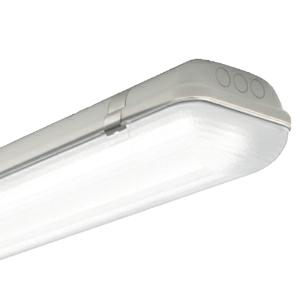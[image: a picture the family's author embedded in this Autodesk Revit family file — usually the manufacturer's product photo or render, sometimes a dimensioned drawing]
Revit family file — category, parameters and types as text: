
# Revit family: 3f_filippi_-_3f_linda_soft_3f_filippi_-_58753_-_3f_linda_led_soft_2x22w_dali_l1570
name_source: partatom
category: Lighting Fixtures
units: mm (PartAtom-declared; Revit-internal decimal feet)

## family parameters
Cut with Voids When Loaded = No
Host = Face
Light Source = No
Part Type = Normal
Room Calculation Point = No
Round Connector Dimension = Use Diameter
Shared = No

## types (1)
- 3F Filippi - 3F Linda Soft (1 x LED, 6835 lm, 49 W, 4000 K)
    Apparent Load = 49 VA
    Approval mark = CE
    CIE Flux Codes = 42 72 91 93 100
    Color Rendering = 80
    Color Temperature = 4000 K
    Control Gear = Electronic transformer
    Default Elevation = 1800 mm
    Description = ILLUMINOTECHNICAL
Luminous efficiency 100% (DLOR 93%, ULOR 7%).
Initial luminous flux of the luminaire 6835 lm.
Direct symmetric distribution.
Installation Interdistance Transv.D = 1.35 x hu - Long.D = 1.24 x hu.
Tabular UGR (CIE 117 - 4H-8H; S=0.25H; 70/50/20): RUG 23.7 - 21.8.
Beam angle: 131° - 111°.
Luminous efficacy 139 lm/W.
Lifetime (L93/B10): 30000 h. (tq+25°C)
Lifetime (L90/B10): 50000 h. (tq+25°C)
Lifetime (L85/B10): 80000 h. (tq+25°C)
Lifetime (L80/B10): 100000 h. (tq+25°C)
Lifetime (L85/B10): 50000 h. (tq+40°C)
Sudden decreased luminous flux after 50000 hours: 0% (C0).
Photobiological safety in compliance with IEC/TR 62778: RG0 risk exempt, (IEC 62471).
In compliance with IEC/EN 62722-2-1 - IEC/EN 62717 standards.

SOURCE
2 linear LED modules 22W/840.
Energy efficiency class (UE 2019/2020 - UE 2019/2015): D.
CIE 13.3 Colour rendering index: CRI >80 (R9 <50%).
IES TM-30 Fidelity Index: Rf = 84 Rg = 95.
CCT nominal colour temperature 4000 K.
Colour initial tolerance (MacAdam): SDCM 3.

MECHANICAL
Self-extinguishing V2 polycarbonate housing, injection moulded, RAL 7035 grey.
Ecologic anti-aging injected sealing gasket.
Soft opal diffuser in self-extinguishing V2 polycarbonate, photo-engraved interior, UV stabilised, injection moulded.
Gear-holder reflector in hot-dip galvanised steel, painted with white polyester base.
Snug fit safety snap-lock clips for diffuser mounting in stainless steel, screwdriver opening.
Fixing brackets in stainless steel.
Possibility for technicians to access the interior of the luminaire.
Luminaire with limited surface temperature. - D - (EN 60598-2-24)
Dimensions: 1570x160 mm, height 100 mm. Weight 3.18 kg.
IP66 protection degree.
Mechanical strength to impacts IK10 (20 joule).
Glow-wire test resistance 850°C.

ELECTRICAL
Halogen Free DALI-2 DATI (Parts 251, 252, 253), PUSH-DIM, electronic wiring 230V-50/60Hz, power factor 0.95 at full load, THD <25%, constant output current, SELV, class I, 1 driver, 1 DALI addresse.
Power of the luminaire 49 W.
ENEC - CE.
SAFE FLICKER: PstLM=<1 and SVM=<0.4 (IEC TR 61547-1 and IEC TR 63158), to ensure a more comfortable and safe light.
Luminaire compliant with EN 60598-2-22 for power supply from a centralised emergency system CPSS (Central Power Supply System), not incorporated in the luminaire - high risk areas excluded. The default power and flux are 100% in AC and 15% in DC.
Ambient temperature from -20°C to +40°C.
Temperature class T6 max 85°C.
Relative humidity UR: <85%.

INSTALLATION
Ceiling / Suspended / Wall.
All accessories dedicated to this product are available on the Catalog and on our website www.3F-Filippi.com.

APPLICATIONS
Suitable product for food production plants (HACCP), IFS (Food Version 6), BRC (GSFS Food Version 7).
Dry, dusty indoor environments, subject to occasional water splashes.
Luminaires designed for diffuse direct/indirect lighting suitable to provide optimum visual comfort.
Transit areas, stairwells.
Virtually shatterproof polycarbonate compatibly with the fumes / atmospheres that compromise the elasticity of plastic materials.
Suitable for illumination of public car parks and parking grounds referred to DIN 67528:2018-04.

LIGHT MANAGEMENT
Recommended minimum setting: 10%.
The luminaire, equipped with (DALI-2 DATI) driver, can be controlled manually with 3F Easy Dim technology or automatically/manually with wired or wireless DALI/D2D control systems.
The D2D driver guarantees interoperability with other devices with the same certification by making the following information available:
Device Data (Part 251), Energy Report (Part 252), Diagnosis & Maintenance (Part 253).
In electrical systems without a regulation system (manual or automatic) and DALI bus, a suitable jumper must be made on the DA-DA terminals of the appliance.

WARNING
Fixture not suitable for cold stores with an ambient temperature <0°C and/or relative humidity >85%.
Luminaire designed for disposal/recycling at end-of-life.
Replaceable (LED only) light source by a professional. Replaceable control gear by a professional.
    Height = 100 mm  [stored 0.328084 ft]
    Lamp = 1 x LED
    Lamp Light Flux = 6835 lm
    Lamp Power = 49 W
    Lamp count = 1
    Length = 1570 mm
    Lifetime = 50000 h
    Luminous efficacy = 139 lm/W
    Manufacturer = 3F Filippi
    ModVariant = No
    Model = 3F Filippi - 58753 - 3F Linda LED Soft 2x22W DALI L1570
    Mounting Place = Ceiling
    Mounting Type = Pendant
    Number of Poles = 1
    OnlyDefault = Yes
    Power Factor = 1
    Product Name = 3F Filippi - 3F Linda Soft
    Product group = pendant luminaire
    ProductGroupID = 9
    Protection Class = Protection class I
    Protection Degree = IP 66
    RLX_Detail_Level = 1
    RLX_Emergency_Light_Flux = 0 lm
    RLX_Emergency_Type = 0
    RLX_Emergency_Type_DB = No
    RlxData = <blob elided: 71713 chars, md5=7a44670f>
    Socket = socket
    Standby Power = 0 W
    System Light Flux = 6835 lm
    System Power = 49 W
    Type Comments = Product without accessories
    Type Image = 3ffilippi_3f_linda_led_soft_2x.jpg
    URL = http://relux.com
    VarID = ---
    Voltage = 0 V
    Weight = 0.00 kg
    Width = 160 mm

note: [stored X ft] marks values corroborated as IEEE doubles in the binary element streams (Revit-internal decimal feet)

## geometry (parser evidence)
native form markers: Blend x4, Sweep x11
no freeform markers — native parametric forms only
